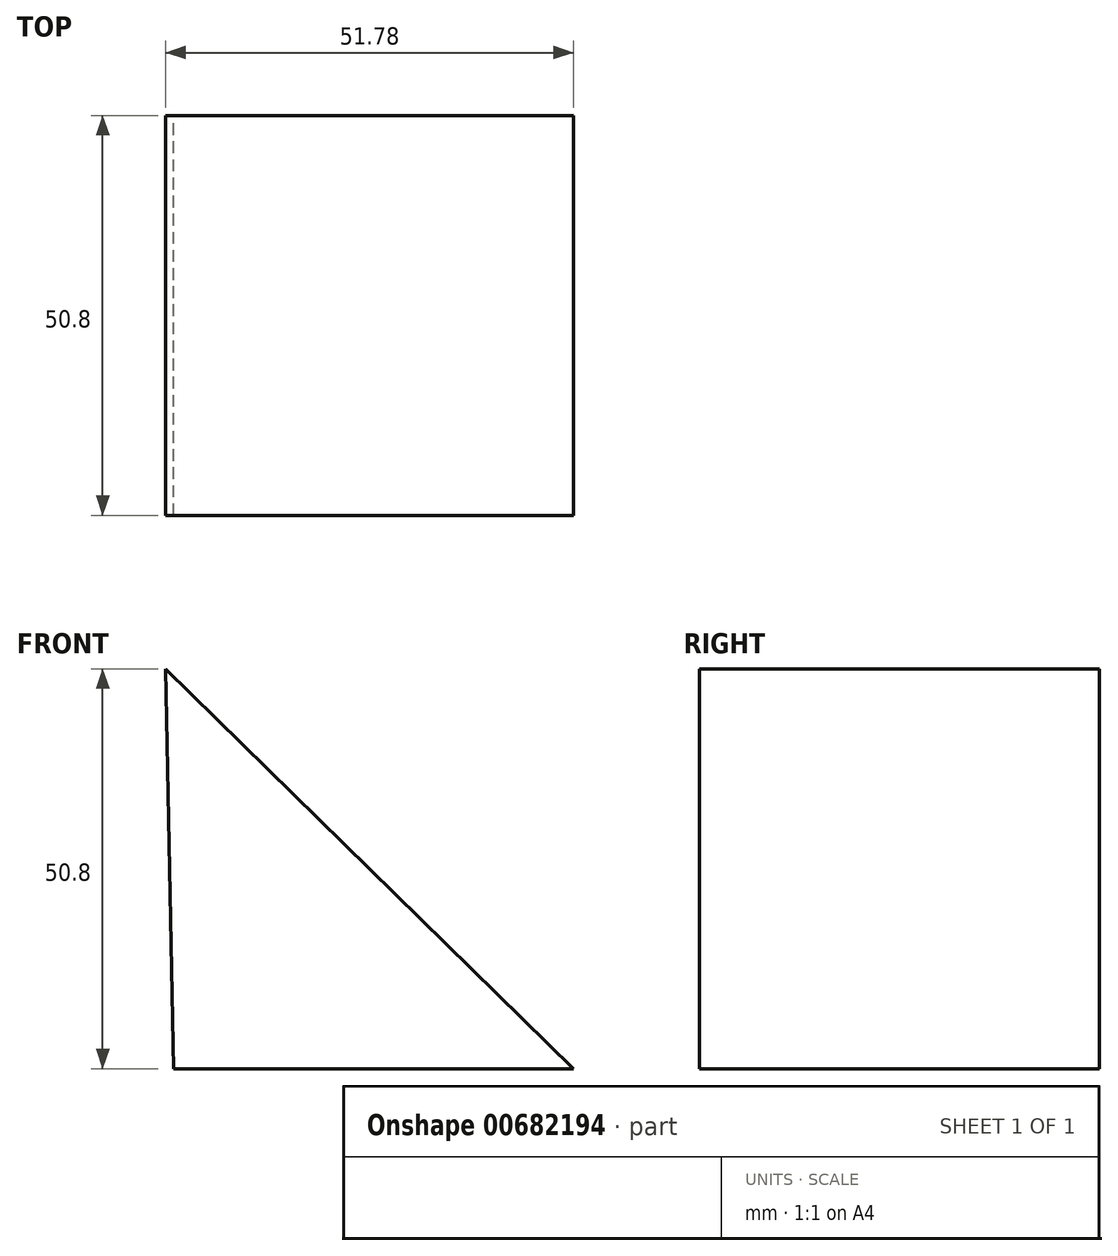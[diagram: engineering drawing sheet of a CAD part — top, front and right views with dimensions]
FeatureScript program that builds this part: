
annotation { "Feature Type Name" : "Feature", "Feature Type Description" : "" }
export const myFeature = defineFeature(function(context is Context, id is Id, definition is map)
    precondition{}
    {
        {
            var Q0;
            Q0=qCreatedBy(makeId("Front.planeOp"),FACE);
            var sketch = newSketch(context, id + "F0", { "sketchPlane" : qUnion([Q0])});
            skLineSegment(sketch, "E0", {"start": v(-51.78, 48.03) * mm, "end": v(-50.8, -2.77) * mm});
            skLineSegment(sketch, "E1", {"start": v(-50.8, -2.77) * mm, "end": v(0, -2.77) * mm});
            skLineSegment(sketch, "E2", {"start": v(-51.78, 48.03) * mm, "end": v(0, -2.77) * mm});
            skSolve(sketch);
        }
        {
            var Q0;
            Q0 = qSketchRegion(id + "F0", true);
            extrude(context, id + "F1", {"entities" : qUnion([Q0]), "depth" : 50.8 * mm, "offsetDistance" : 25.4 * mm});
        }
    });
